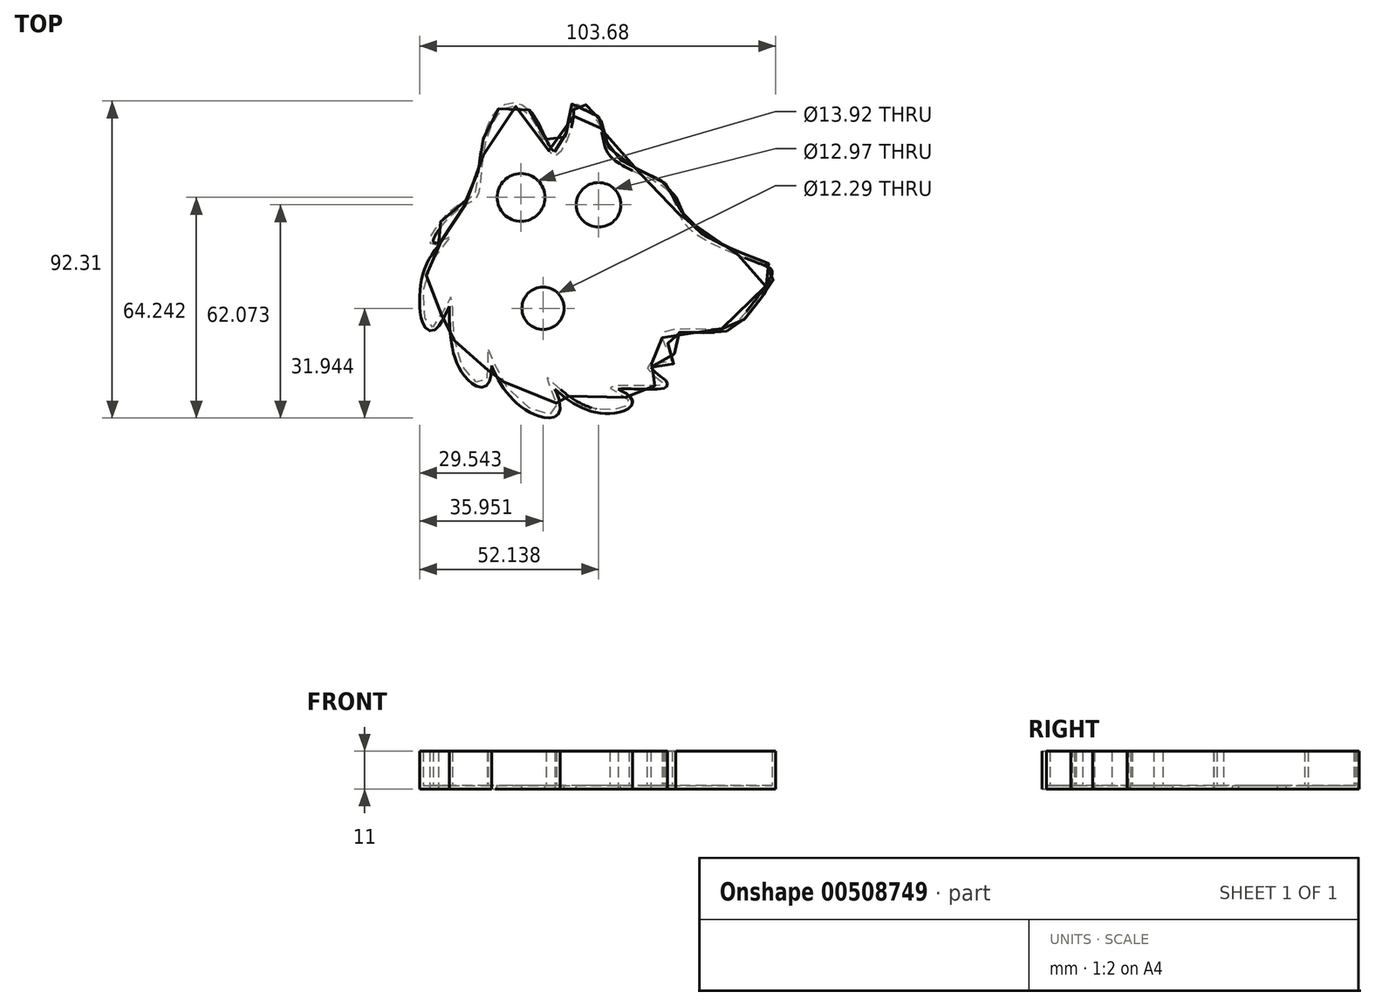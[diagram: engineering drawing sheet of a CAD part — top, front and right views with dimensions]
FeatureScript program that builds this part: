
annotation { "Feature Type Name" : "Feature", "Feature Type Description" : "" }
export const myFeature = defineFeature(function(context is Context, id is Id, definition is map)
    precondition{}
    {
        {
            var Q0;
            Q0=qCreatedBy(makeId("Top.planeOp"),FACE);
            var sketch = newSketch(context, id + "F0", { "sketchPlane" : qUnion([Q0])});
            skFitSpline(sketch, "E0", {"points": [v(32.61, -20.57) * mm, v(16.15, -21.49) * mm, v(15.85, -25.15) * mm, v(17.98, -30.02) * mm, v(10.97, -31.24) * mm, v(14.33, -35.5) * mm, v(15.54, -37.03) * mm, v(0, -37.64) * mm, v(5.49, -41.6) * mm, v(-6.1, -43.43) * mm, v(-18.6, -34.9) * mm, v(-15.54, -44.35) * mm, v(-28.04, -40.08) * mm, v(-35.66, -26.37) * mm, v(-36.27, -36.12) * mm, v(-44.2, -28.8) * mm, v(-46.33, -11.43) * mm, v(-51.82, -20.27) * mm, v(-52.73, -2.9) * mm, v(-46.02, 6.25) * mm, v(-51.2, 4.42) * mm, v(-43.9, 14.48) * mm, v(-38.7, 17.53) * mm, v(-36.58, 31.55) * mm, v(-30.18, 43.74) * mm, v(-23.77, 41.91) * mm, v(-18.29, 31.85) * mm, v(-15.24, 30.02) * mm, v(-10.67, 40.7) * mm, v(-9.75, 44.65) * mm, v(-3.35, 39.17) * mm, v(0, 29.72) * mm, v(15.85, 20.57) * mm, v(19.5, 14.17) * mm, v(25.6, 6.55) * mm, v(45.11, -2.29) * mm, v(47.24, -4.42) * mm, v(39.93, -15.4) * mm, v(32.61, -20.57) * mm]});
            skSolve(sketch);
        }
        {
            var Q0;
            Q0=makeQuery(id+"F0.imprint","IMPRINT",FACE,{"disambiguationData":[TD([[makeQuery(id+"F0.imprint","IMPRINT",EDGE,{"derivedFrom":sQuery(id+"F0.wireOp",EDGE,"E0")}),-1.0]])]});
            extrude(context, id + "F1", {"entities" : qUnion([Q0]), "depth" : 10 * mm});
        }
        {
            var Q0;
            Q0=makeQuery(id+"F1.opExtrude","CAP_FACE",FACE,{"disambiguationData":[OSD([sQuery(id+"F0.wireOp",EDGE,"E0")])],"isStart":false});
            shell(context, id + "F2", {"entities" : qUnion([Q0]), "thickness" : 1 * mm, "oppositeDirection" : true});
        }
        {
            var Q0;
            Q0=makeQuery(id+"F0.imprint","IMPRINT",FACE,{"disambiguationData":[TD([[makeQuery(id+"F0.imprint","IMPRINT",EDGE,{"derivedFrom":sQuery(id+"F0.wireOp",EDGE,"E0")}),-1.0]])]});
            var sketch = newSketch(context, id + "F3", { "sketchPlane" : qUnion([Q0])});
            skCircle(sketch, "E1", {"center": v(-25.88, 17.6) * mm, "radius": 6.96 * mm});
            skCircle(sketch, "E2", {"center": v(-3.28, 15.42) * mm, "radius": 6.49 * mm});
            skCircle(sketch, "E3", {"center": v(-19.47, -14.7) * mm, "radius": 6.15 * mm});
            skSolve(sketch);
        }
        {
            var Q0;
            Q0 = qSketchRegion(id + "F3", true);
            extrude(context, id + "F4", {"entities" : qUnion([Q0]), "operationType" : NewBodyOperationType.REMOVE, "oppositeDirection" : true, "depth" : 25 * mm});
        }
    });
